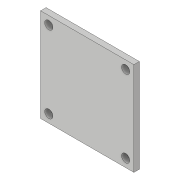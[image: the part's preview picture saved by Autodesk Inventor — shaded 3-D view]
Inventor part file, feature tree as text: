
AUTODESK INVENTOR PART (.ipt)
format: ipt  version: 2019 (Build 230136000, 136)  size: 95,744 bytes
history: native  units: mm
features: extrude x2, sketch x2
ambient origin geometry x8: Origin, YZ Plane, XZ Plane, XY Plane, X Axis, Y Axis, Z Axis, Center Point
bodies: Solid1 (feature_tree)
feature tree (4):
  extrude  "Extrusion1"  Depth=170.0mm
  extrude  "Extrusion2"  Depth=10.0mm
  sketch  "Sketch1"  dims[d0=170.0mm d1=170.0mm]
  sketch  "Sketch2"  dims[d2=10.0mm d3=0.0mm d4=15.0mm d5=15.0mm d6=155.0mm d7=140.0mm d8=140.0mm d9=140.0mm d10=15.0mm d11=15.0mm d12=15.0mm d13=15.0mm d14=10.0mm d15=0.0mm]
